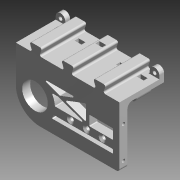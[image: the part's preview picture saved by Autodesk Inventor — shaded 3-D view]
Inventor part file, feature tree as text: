
AUTODESK INVENTOR PART (.ipt)
format: ipt  version: 2015 (Build 190159000, 159)  size: 297,984 bytes
history: native  units: mm (DEFAULTED — no unit token found)
features: other x11, fillet x1
bodies: Body1 (feature_tree)
feature tree (12):
  other  "combined_base_caterpillar_narrow_B.iam"
  other  "support_caterpillar_top_v3_narrow.ipt:1"
  other  "support_caterpillar_lateral_v3_Right.ipt:1"
  other  "Sólido1"
  other  "Origen"
  fillet  "Empalme1"  Radius=10.0mm
  other  "Plano YZ"
  other  "Plano XZ"
  other  "Plano XY"
  other  "Eje X"
  other  "Eje Y"
  other  "Eje Z"
